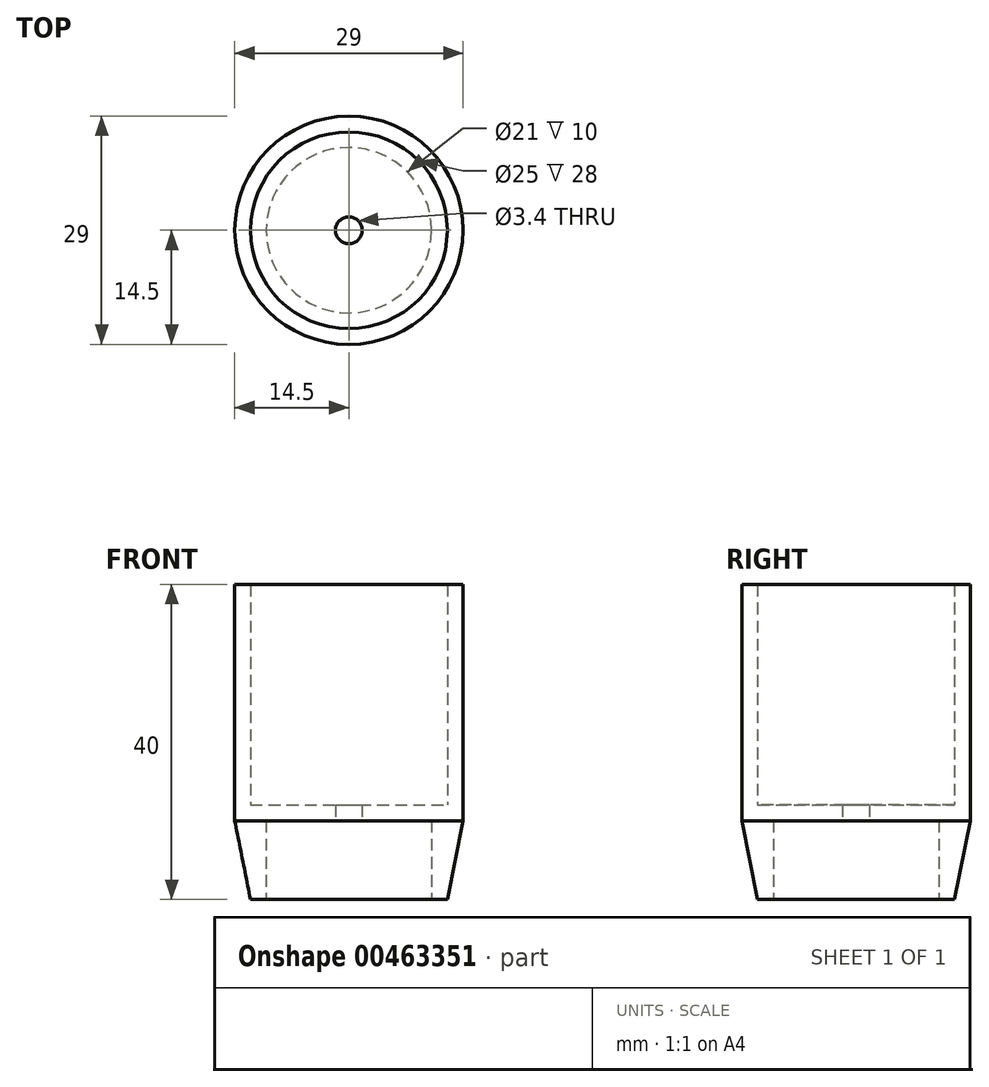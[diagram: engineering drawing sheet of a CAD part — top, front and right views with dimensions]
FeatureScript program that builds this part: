
annotation { "Feature Type Name" : "Feature", "Feature Type Description" : "" }
export const myFeature = defineFeature(function(context is Context, id is Id, definition is map)
    precondition{}
    {
        {
            var Q0;
            Q0=qCreatedBy(makeId("Front.planeOp"),FACE);
            var sketch = newSketch(context, id + "F0", { "sketchPlane" : qUnion([Q0])});
            skLineSegment(sketch, "E0", {"start": v(0, 0) * mm, "end": v(0, 40) * mm, "construction": true});
            skLineSegment(sketch, "E1", {"start": v(10.5, 10) * mm, "end": v(1.7, 10) * mm});
            skLineSegment(sketch, "E2", {"start": v(1.7, 10) * mm, "end": v(1.7, 12) * mm});
            skLineSegment(sketch, "E3", {"start": v(1.7, 12) * mm, "end": v(12.5, 12) * mm});
            skLineSegment(sketch, "E4", {"start": v(12.5, 12) * mm, "end": v(12.5, 40) * mm});
            skLineSegment(sketch, "E5", {"start": v(12.5, 40) * mm, "end": v(14.5, 40) * mm});
            skLineSegment(sketch, "E6", {"start": v(14.5, 40) * mm, "end": v(14.5, 10) * mm});
            skLineSegment(sketch, "E7", {"start": v(14.5, 10) * mm, "end": v(12.5, 0) * mm});
            skLineSegment(sketch, "E8", {"start": v(12.5, 0) * mm, "end": v(10.5, 0) * mm});
            skLineSegment(sketch, "E9", {"start": v(10.5, 0) * mm, "end": v(10.5, 10) * mm});
            skSolve(sketch);
        }
        {
            var Q0;
            Q0=makeQuery(id+"F0.imprint","IMPRINT",FACE,{"disambiguationData":[TD([[makeQuery(id+"F0.imprint","IMPRINT",EDGE,{"derivedFrom":sQuery(id+"F0.wireOp",EDGE,"E1")}),-1.0]])]});
            var Q1;
            Q1=sQuery(id+"F0.wireOp",EDGE,"E0");
            revolve(context, id + "F1", {"entities" : qUnion([Q0]), "axis" : qUnion([Q1]), "revolveType" : RevolveType.FULL});
        }
    });
